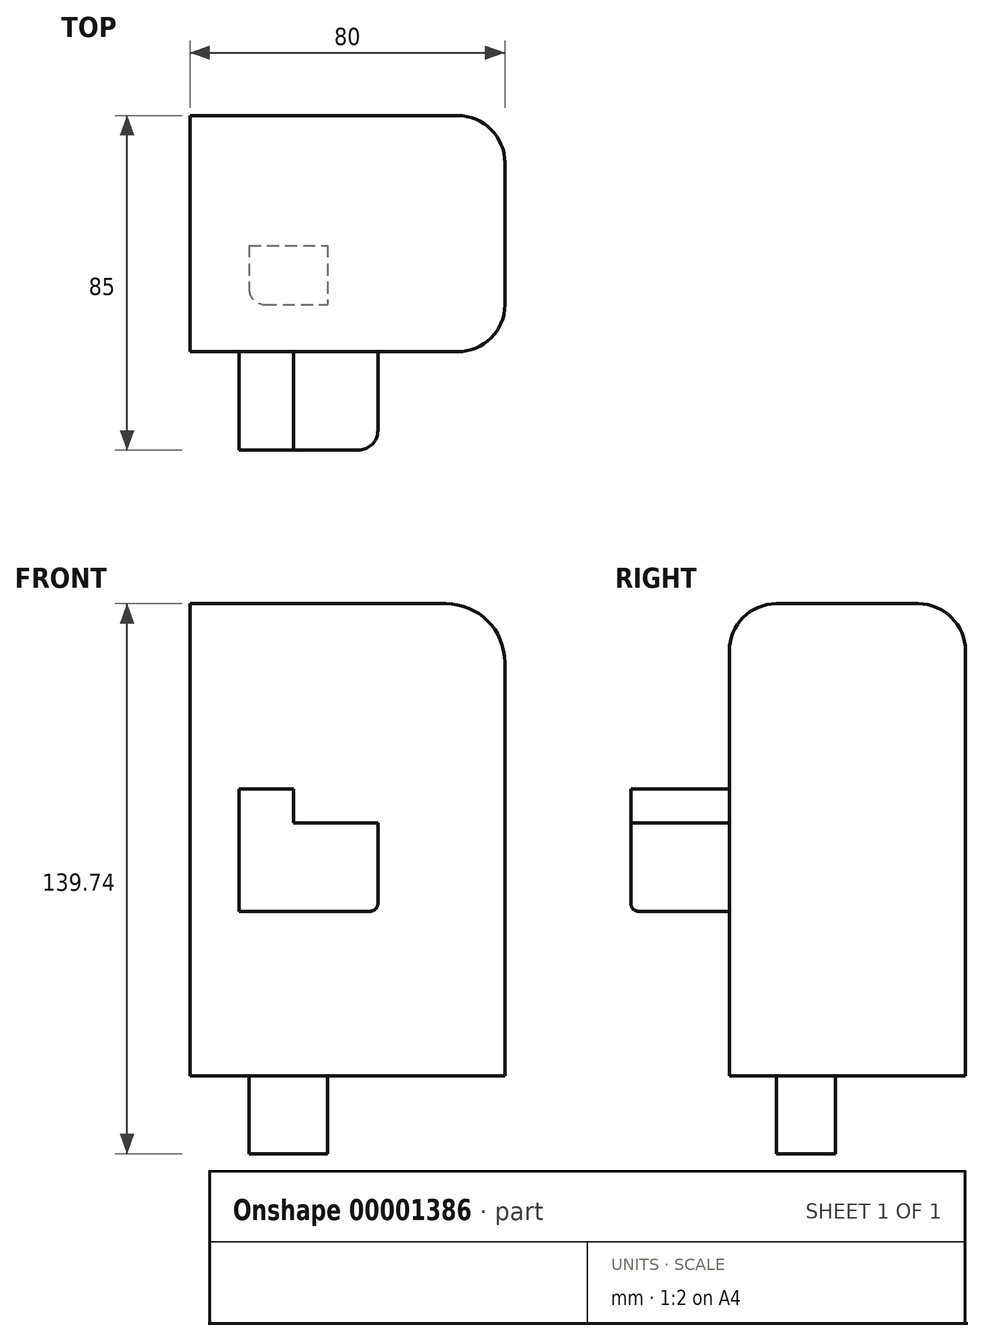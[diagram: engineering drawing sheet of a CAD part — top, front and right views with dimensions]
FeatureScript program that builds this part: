
annotation { "Feature Type Name" : "Feature", "Feature Type Description" : "" }
export const myFeature = defineFeature(function(context is Context, id is Id, definition is map)
    precondition{}
    {
        {
            var Q0;
            Q0=qCreatedBy(makeId("Top.planeOp"),FACE);
            var sketch = newSketch(context, id + "F0", { "sketchPlane" : qUnion([Q0])});
            skLineSegment(sketch, "E0.bottom", {"start": v(0, 0) * mm, "end": v(80, 0) * mm});
            skLineSegment(sketch, "E0.top", {"start": v(0, 60) * mm, "end": v(80, 60) * mm});
            skLineSegment(sketch, "E0.left", {"start": v(0, 0) * mm, "end": v(0, 60) * mm});
            skLineSegment(sketch, "E0.right", {"start": v(80, 0) * mm, "end": v(80, 60) * mm});
            skSolve(sketch);
        }
        {
            var Q0;
            Q0 = qSketchRegion(id + "F0", true);
            extrude(context, id + "F1", {"entities" : qUnion([Q0]), "depth" : 120 * mm});
        }
        {
            var Q0;
            Q0=makeQuery(id+"F1.opExtrude","CAP_EDGE",EDGE,{"disambiguationData":[OSD([sQuery(id+"F0.wireOp",EDGE,"E0.right")])],"isStart":false});
            fillet(context, id + "F2", {"entities" : qUnion([Q0]), "radius" : 15 * mm, "tangentPropagation" : true, "allowEdgeOverflow" : false});
        }
        {
            var Q0;
            Q0=makeQuery(id+"F1.opExtrude","CAP_EDGE",EDGE,{"disambiguationData":[OSD([sQuery(id+"F0.wireOp",EDGE,"E0.top")])],"isStart":false});
            var Q1;
            Q1=makeQuery(id+"F1.opExtrude","CAP_EDGE",EDGE,{"disambiguationData":[OSD([sQuery(id+"F0.wireOp",EDGE,"E0.bottom")])],"isStart":false});
            fillet(context, id + "F3", {"entities" : qUnion([Q0, Q1]), "radius" : 12 * mm, "tangentPropagation" : true, "defaultsChanged" : true, "vertexSettings" : [], "allowEdgeOverflow" : false});
        }
        {
            var Q0;
            Q0=makeQuery(id+"F1.opExtrude","SWEPT_FACE",FACE,{"disambiguationData":[OSD([sQuery(id+"F0.wireOp",EDGE,"E0.bottom")])]});
            var sketch = newSketch(context, id + "F4", { "sketchPlane" : qUnion([Q0])});
            skLineSegment(sketch, "E1", {"start": v(12.42, 41.83) * mm, "end": v(47.72, 41.83) * mm});
            skLineSegment(sketch, "E2", {"start": v(47.72, 41.83) * mm, "end": v(47.72, 64.35) * mm});
            skLineSegment(sketch, "E3", {"start": v(47.72, 64.35) * mm, "end": v(26.32, 64.35) * mm});
            skLineSegment(sketch, "E4", {"start": v(26.32, 64.35) * mm, "end": v(26.32, 72.95) * mm});
            skLineSegment(sketch, "E5", {"start": v(26.32, 72.95) * mm, "end": v(12.42, 72.95) * mm});
            skLineSegment(sketch, "E6", {"start": v(12.42, 72.95) * mm, "end": v(12.42, 41.83) * mm});
            skSolve(sketch);
        }
        {
            var Q0;
            Q0 = qSketchRegion(id + "F4", true);
            extrude(context, id + "F5", {"entities" : qUnion([Q0]), "operationType" : NewBodyOperationType.ADD, "depth" : 25 * mm});
        }
        {
            var Q0;
            Q0=makeQuery(id+"F5.opExtrude","CAP_EDGE",EDGE,{"disambiguationData":[OSD([sQuery(id+"F4.wireOp",EDGE,"E2")])],"isStart":false});
            fillet(context, id + "F6", {"entities" : qUnion([Q0]), "radius" : 5 * mm, "tangentPropagation" : true, "allowEdgeOverflow" : false});
        }
        {
            var Q0;
            Q0=makeQuery(id+"F5.opExtrude","CAP_EDGE",EDGE,{"disambiguationData":[OSD([sQuery(id+"F4.wireOp",EDGE,"E1")])],"isStart":false});
            fillet(context, id + "F7", {"entities" : qUnion([Q0]), "radius" : 2 * mm, "tangentPropagation" : true, "allowEdgeOverflow" : false});
        }
        {
            var Q0;
            Q0=makeQuery(id+"F1.opExtrude","CAP_FACE",FACE,{"disambiguationData":[OSD([sQuery(id+"F0.wireOp",EDGE,"E0.bottom"),sQuery(id+"F0.wireOp",EDGE,"E0.top"),sQuery(id+"F0.wireOp",EDGE,"E0.left"),sQuery(id+"F0.wireOp",EDGE,"E0.right")])],"isStart":true});
            var sketch = newSketch(context, id + "F8", { "sketchPlane" : qUnion([Q0])});
            skLineSegment(sketch, "E7.bottom", {"start": v(15, -27) * mm, "end": v(35, -27) * mm});
            skLineSegment(sketch, "E7.top", {"start": v(19, -12) * mm, "end": v(35, -12) * mm});
            skLineSegment(sketch, "E7.left", {"start": v(15, -27) * mm, "end": v(15, -16) * mm});
            skLineSegment(sketch, "E7.right", {"start": v(35, -27) * mm, "end": v(35, -12) * mm});
            skPoint(sketch, "E8.visualSharp", {"position": v(15, -12) * mm});
            skArc(sketch, "E8.filletArc", {"start": v(19, -12) * mm, "mid": v(16.17, -13.17) * mm, "end": v(15, -16) * mm});
            skSolve(sketch);
        }
        {
            var Q0;
            Q0 = qSketchRegion(id + "F8", true);
            extrude(context, id + "F9", {"entities" : qUnion([Q0]), "operationType" : NewBodyOperationType.ADD, "depth" : 19.74 * mm});
        }
    });
